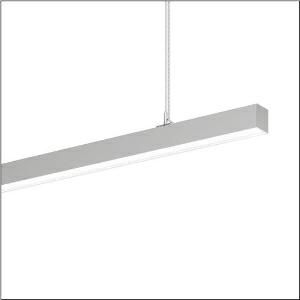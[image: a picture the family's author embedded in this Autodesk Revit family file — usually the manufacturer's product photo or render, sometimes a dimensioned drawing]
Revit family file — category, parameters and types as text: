
# Revit family: silica_r__21_51mx33dc3dsb_c168
name_source: partatom
category: Lighting Fixtures
units: mm (PartAtom-declared; Revit-internal decimal feet)

## family parameters
Cut with Voids When Loaded = No
Host = Face
Light Source = No
Part Type = Normal
Room Calculation Point = No
Round Connector Dimension = Use Diameter
Shared = No

## types (1)
- --- (1 x LED, 14780 lm, 99.5 W, 3000K)
    Apparent Load = 100 VA
    CIE Flux Codes = 78 96 99 55 100
    Color Rendering = 80
    Color Temperature = 3000K
    Default Elevation = 1800 mm
    Description = Silica® 21, office luminaire, primary optical cover: prismatic diffuser, of PMMA, CAT 2 (L<= 3000cd/m²), light emission: direct/indirect distribution, primary light characteristic: symmetric, installation type: suspended mounting, LED, rated luminous flux: 14.780lm, luminous efficacy: 149lm/W, light colour: 830, colour temperature: 3000K, with terminal, 3+2-pole, max. 2.5mm², mains connection: 220..240V, AC, 50/60Hz, rated input power: 99.5W, luminaire housing, of aluminium, metallic grey (RAL 9006), length: 3.004mm, width: 53mm, height: 53mm, protection rating (complete): IP20, insulation class (complete): insulation class I (protective earthing), certification: CE, permissible operating ambient temperature: 0..+35°C, standard: EN 50419, packaging unit: 1 piece
    Height = 53 mm
    Lamp = 1 x LED
    Lamp Light Flux = 14780 lm
    Lamp Power = 99.5 W
    Lamp count = 1
    Length = 3004 mm
    Luminous efficacy = 149 lm/W
    Manufacturer = Siteco
    ModVariant = No
    Model = 51MX33DC3DSB
    Mounting Place = Ceiling
    Mounting Type = Pendant
    Number of Poles = 1
    OnlyDefault = Yes
    Power Factor = 1
    Product Name = Silica® 21
    Product group = office luminaire | ceiling pendant
    ProductGroupID = 902
    Protection Class = Protection class I
    Protection Degree = IP 20
    RLX_Detail_Level = 1
    RLX_Emergency_Light_Flux = 0 lm
    RLX_Emergency_Type = 0
    RLX_Emergency_Type_DB = No
    RlxData = <blob elided: 23453 chars, md5=6b33fd49>
    Socket = socket
    Standby Power = 0 W
    System Light Flux = 14780 lm
    System Power = 100 W
    Type Comments = factory setting: luminous flux: 100 % | dim-lin: 254 | 345 mA
    Type Image = l_1313621.jpg
    URL = http://relux.com
    VarID = @adj_066979
    Voltage = 0 V
    Weight = 0.00 kg
    Width = 53 mm

## geometry (parser evidence)
native form markers: Blend x4, Sweep x12
no freeform markers — native parametric forms only
